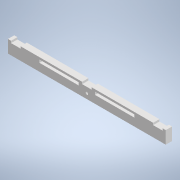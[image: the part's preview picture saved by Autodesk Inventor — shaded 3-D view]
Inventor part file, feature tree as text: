
AUTODESK INVENTOR PART (.ipt)
format: ipt  version: 2022 (Build 260153000, 153)  size: 135,680 bytes
history: native  units: mm
features: extrude x1, sketch x1
ambient origin geometry x8: Origin, YZ Plane, XZ Plane, XY Plane, X Axis, Y Axis, Z Axis, Center Point
bodies: Body1 (feature_tree)
feature tree (2):
  extrude  "Extrusion5"  Depth=20.0mm
  sketch  "Sketch1"  dims[d0=250.0mm d1=20.0mm d20=150.0mm d21=4.5mm d22=4.5mm d32=4.0mm d33=2.0mm d36=13.0mm d39=3.2mm d40=5.0mm d41=15.0mm d42=3.2mm d44=7.5mm d45=3.2mm d46=0.0mm]
